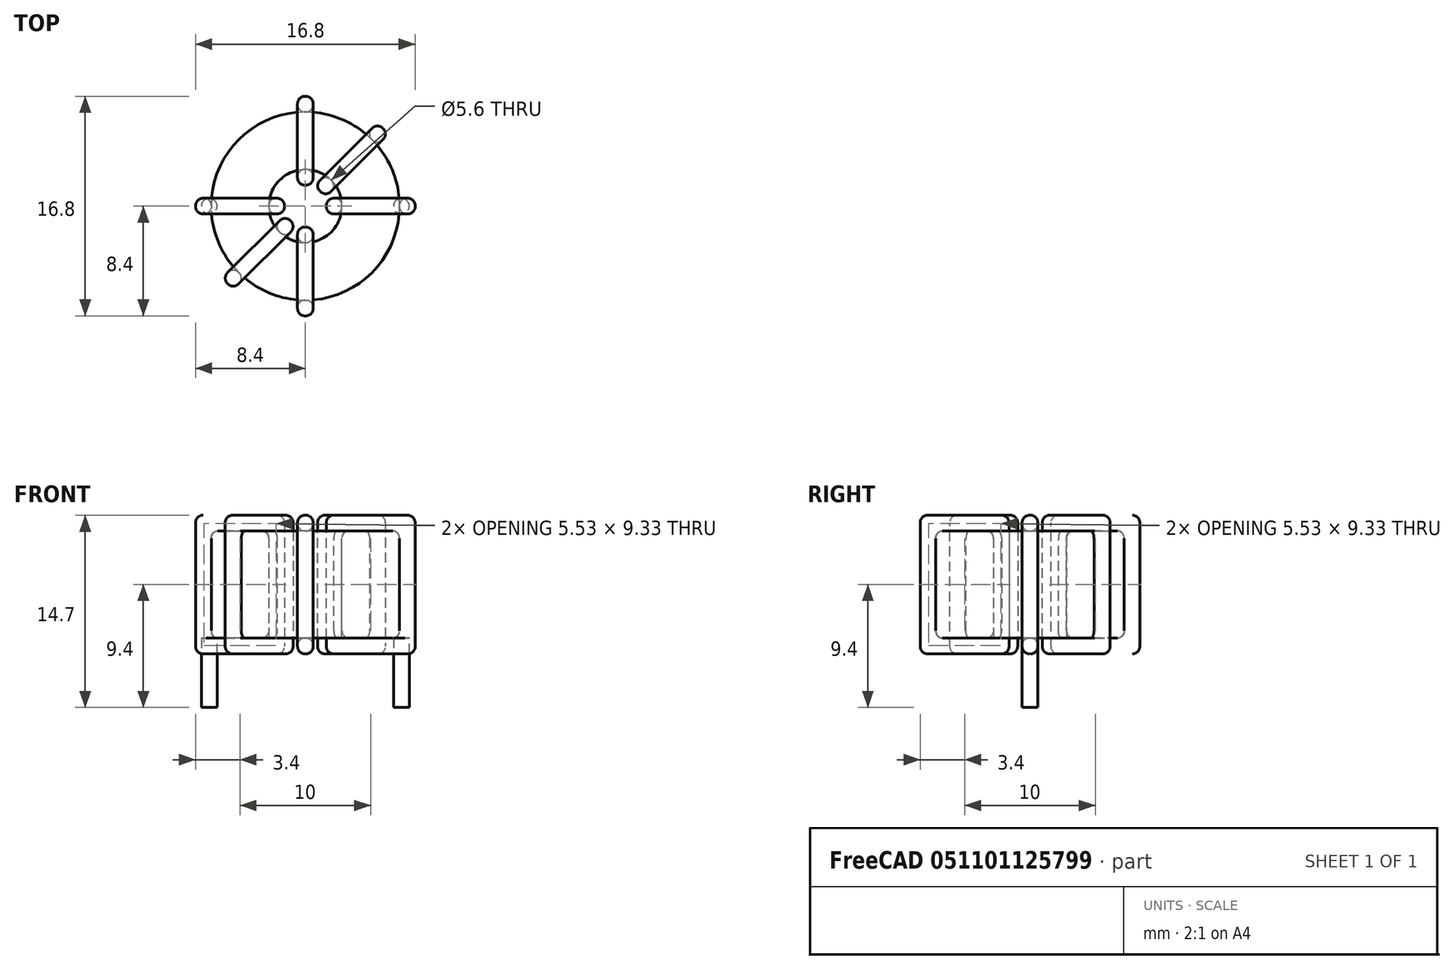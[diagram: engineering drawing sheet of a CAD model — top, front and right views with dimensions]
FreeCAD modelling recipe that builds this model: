
FCSTD DOCUMENT  (FreeCAD 0.16R6703 (Git))
Label: L_Toroid_Horizontal_D16.8mm_P14.70mm_Vishay_TJ3_BigPads
License: All rights reserved
LicenseURL: http://en.wikipedia.org/wiki/All_rights_reserved
objects: Sketcher::SketchObject×6, PartDesign::Pad×6, PartDesign::Fillet×5, Spreadsheet::Sheet×1
note: 23 computed .brp shape members not serialized (recipe doc carries the construction recipe); baked Part::Feature solids carry a one-line shape summary decoded from their .brp

FEATURE [Spreadsheet::Sheet] Spreadsheet  label="dimensions"
  cells = A1=Wx; B1(Wx)=16.8; C1(WW)=5.600000000000001; D1=16.8; A2=Wy; B2(Wy)=16.8; D2=16.8; A3=RM; B3(RMx)=14.7; C3(RMy)=0; A4=d_wire; B4(d_wire)=1.2; A5=H; B5(H)=8.199999999999999; A6=offsetx; B6(offsetx)=1.050000000000001
FEATURE [Sketcher::SketchObject] Sketch
  Placement = pos=(0,0,1.7) rot=(0,0,1;0rad)
  expr: Placement.Base.z = 0.5 + Spreadsheet.d_wire
  expr: Constraints[0] = Spreadsheet.Wx / 2 - Spreadsheet.d_wire
  expr: Constraints[4] = Spreadsheet.WW / 2
  expr: Constraints[2] = Spreadsheet.RMy / 2
  expr: Constraints[1] = Spreadsheet.RMx / 2
  sketch-geometry (2):
    g0: Circle CenterX=7.35 CenterY=0 CenterZ=0 NormalX=0 NormalY=0 NormalZ=1 Radius=7.2
    g1: Circle CenterX=7.35 CenterY=0 CenterZ=0 NormalX=0 NormalY=0 NormalZ=1 Radius=2.8
  constraints (5):
    c: Radius(g0) = 7.2
    c: DistanceX(g-1,g0) = 7.35
    c: DistanceY(g-1,g0) = 0
    c: Coincident(g1,g0)
    c: Radius(g1) = 2.8
FEATURE [PartDesign::Pad] Pad
  Length = 8.2
  Length2 = 100
  Placement = pos=(0,0,1.7) rot=(0,0,1;0rad)
  Sketch = -> Sketch
  Type = 0
  expr: Length = Spreadsheet.H
FEATURE [Sketcher::SketchObject] Sketch001
  Placement = pos=(0,0,1.1) rot=(0,0,1;0rad)
  expr: Placement.Base.z = 0.5 + Spreadsheet.d_wire * 0.5
  expr: Constraints[4] = Spreadsheet.RMx
  expr: Constraints[2] = Spreadsheet.RMy
  expr: Constraints[1] = Spreadsheet.d_wire / 2
  sketch-geometry (2):
    g0: Circle CenterX=0 CenterY=0 CenterZ=0 NormalX=0 NormalY=0 NormalZ=1 Radius=0.6
    g1: Circle CenterX=14.7 CenterY=0 CenterZ=0 NormalX=0 NormalY=0 NormalZ=1 Radius=0.6
  constraints (5):
    c: Equal(g0,g1)
    c: Radius(g0) = 0.6
    c: DistanceY(g-1,g1) = 0
    c: Coincident(g0,g-1)
    c: DistanceX(g-1,g1) = 14.7
FEATURE [PartDesign::Pad] Pad001
  Length = 0.6
  Length2 = 4.7
  Placement = pos=(0,0,1.1) rot=(0,0,1;0rad)
  Reversed = true
  Sketch = -> Sketch001
  Type = 4
  expr: Length2 = 3.5 + Spreadsheet.d_wire
  expr: Length = Spreadsheet.d_wire / 2
FEATURE [PartDesign::Fillet] Fillet
  Base = -> Pad [Edge6,Edge3,Edge2]
  Placement = pos=(0,0,1.7) rot=(0,0,1;0rad)
  Radius = 0.5
FEATURE [Sketcher::SketchObject] Sketch003
  Placement = pos=(7.35,0,0) rot=(1,0,0;1.5708rad)
  expr: Placement.Base.x = Spreadsheet.RMx / 2
  expr: Constraints[49] = Spreadsheet.Wx - Spreadsheet.d_wire * 2
  expr: Constraints[44] = Spreadsheet.d_wire
  expr: Constraints[23] = Spreadsheet.H
  expr: Constraints[22] = Spreadsheet.Wx / 2 - Spreadsheet.d_wire
  expr: Placement.Base.y = Spreadsheet.RMy / 2
  expr: Constraints[21] = (Spreadsheet.Wx - Spreadsheet.WW) / 2 - Spreadsheet.d_wire
  expr: Constraints[19] = Spreadsheet.d_wire
  expr: Constraints[17] = Spreadsheet.d_wire
  expr: Constraints[18] = Spreadsheet.d_wire
  expr: Constraints[16] = Spreadsheet.d_wire
  sketch-geometry (16):
    g0: LineSegment StartX=-1.6 StartY=0.5 StartZ=0 EndX=-8.4 EndY=0.5 EndZ=0
    g1: LineSegment StartX=-8.4 StartY=0.5 StartZ=0 EndX=-8.4 EndY=11.1 EndZ=0
    g2: LineSegment StartX=-8.4 StartY=11.1 StartZ=0 EndX=-1.6 EndY=11.1 EndZ=0
    g3: LineSegment StartX=-1.6 StartY=11.1 StartZ=0 EndX=-1.6 EndY=0.5 EndZ=0
    g4: LineSegment StartX=-7.2 StartY=9.9 StartZ=0 EndX=-2.8 EndY=9.9 EndZ=0
    g5: LineSegment StartX=-2.8 StartY=9.9 StartZ=0 EndX=-2.8 EndY=1.7 EndZ=0
    g6: LineSegment StartX=-2.8 StartY=1.7 StartZ=0 EndX=-7.2 EndY=1.7 EndZ=0
    g7: LineSegment StartX=-7.2 StartY=1.7 StartZ=0 EndX=-7.2 EndY=9.9 EndZ=0
    g8: LineSegment StartX=1.6 StartY=11.1 StartZ=0 EndX=8.4 EndY=11.1 EndZ=0
    g9: LineSegment StartX=8.4 StartY=11.1 StartZ=0 EndX=8.4 EndY=0.5 EndZ=0
    g10: LineSegment StartX=8.4 StartY=0.5 StartZ=0 EndX=1.6 EndY=0.5 EndZ=0
    g11: LineSegment StartX=1.6 StartY=0.5 StartZ=0 EndX=1.6 EndY=11.1 EndZ=0
    g12: LineSegment StartX=2.8 StartY=9.9 StartZ=0 EndX=7.2 EndY=9.9 EndZ=0
    g13: LineSegment StartX=7.2 StartY=9.9 StartZ=0 EndX=7.2 EndY=1.7 EndZ=0
    g14: LineSegment StartX=7.2 StartY=1.7 StartZ=0 EndX=2.8 EndY=1.7 EndZ=0
    g15: LineSegment StartX=2.8 StartY=1.7 StartZ=0 EndX=2.8 EndY=9.9 EndZ=0
  constraints (50):
    c: Horizontal(g0)
    c: Coincident(g1,g0)
    c: Vertical(g1)
    c: Coincident(g2,g1)
    c: Horizontal(g2)
    c: Coincident(g3,g2)
    c: Coincident(g3,g0)
    c: Vertical(g3)
    c: Coincident(g4,g5)
    c: Coincident(g5,g6)
    c: Coincident(g6,g7)
    c: Coincident(g7,g4)
    c: Horizontal(g4)
    c: Horizontal(g6)
    c: Vertical(g5)
    c: Vertical(g7)
    c: DistanceX(g1,g4) = 1.2
    c: DistanceY(g4,g1) = 1.2
    c: DistanceX(g5,g0) = 1.2
    c: DistanceY(g0,g5) = 1.2
    c: DistanceY(g-1,g0) = 0.5
    c: DistanceX(g6,g6) = 4.4
    c: DistanceX(g6,g-1) = 7.2
    c: DistanceY(g7,g7) = 8.2
    c: Coincident(g8,g9)
    c: Coincident(g9,g10)
    c: Coincident(g10,g11)
    c: Coincident(g11,g8)
    c: Horizontal(g8)
    c: Horizontal(g10)
    c: Vertical(g9)
    c: Vertical(g11)
    c: Coincident(g12,g13)
    c: Coincident(g13,g14)
    c: Coincident(g14,g15)
    c: Coincident(g15,g12)
    c: Horizontal(g12)
    c: Horizontal(g14)
    c: Vertical(g13)
    c: Vertical(g15)
    c: DistanceY(g8,g2) = 0
    c: DistanceY(g10,g0) = 0
    c: DistanceY(g14,g5) = 0
    c: DistanceY(g12,g4) = 0
    c: DistanceX(g8,g12) = 1.2
    c: Equal(g8,g2)
    c: Equal(g12,g4)
    c: Equal(g9,g1)
    c: Equal(g13,g7)
    c: DistanceX(g4,g12) = 14.4
FEATURE [PartDesign::Pad] Pad002
  Length = 1.2
  Length2 = 100
  Midplane = true
  Placement = pos=(7.35,0,0) rot=(1,0,0;1.5708rad)
  Sketch = -> Sketch003
  Type = 0
  expr: Length = Spreadsheet.d_wire
FEATURE [PartDesign::Fillet] Fillet001
  Base = -> Pad002 [Edge38,Edge41,Edge42,Edge43,Edge29,Edge32,Edge33,Edge34,Edge25,Edge35,Edge36,Edge13,Edge14,Edge15,Edge16,Edge17,Edge18,Edge19,Edge1,Edge2,Edge3,Edge4,Edge5,Edge6,Edge7,Edge37,Edge39,Edge40,Edge20,Edge23,Edge24,Edge21,Edge22,Edge8,Edge9,Edge10,Edge11,Edge12,Edge26,Edge27,+8 more]
  Placement = pos=(7.35,0,0) rot=(1,0,0;1.5708rad)
  Radius = 0.564
  expr: Radius = Spreadsheet.d_wire * 0.47
FEATURE [Sketcher::SketchObject] Sketch004
  Placement = pos=(7.35,0,0) rot=(0.862856,0.357407,0.357407;1.71777rad)
  expr: Placement.Base.x = Spreadsheet.RMx / 2
  expr: Constraints[49] = Spreadsheet.Wx - 2 * Spreadsheet.d_wire
  expr: Constraints[44] = Spreadsheet.d_wire
  expr: Constraints[23] = Spreadsheet.H
  expr: Constraints[22] = Spreadsheet.Wx / 2 - Spreadsheet.d_wire
  expr: Placement.Base.y = Spreadsheet.RMy / 2
  expr: Constraints[21] = (Spreadsheet.Wx - Spreadsheet.WW) / 2 - Spreadsheet.d_wire
  expr: Constraints[19] = Spreadsheet.d_wire
  expr: Constraints[17] = Spreadsheet.d_wire
  expr: Constraints[18] = Spreadsheet.d_wire
  expr: Constraints[16] = Spreadsheet.d_wire
  sketch-geometry (16):
    g0: LineSegment StartX=-1.6 StartY=0.5 StartZ=0 EndX=-8.4 EndY=0.5 EndZ=0
    g1: LineSegment StartX=-8.4 StartY=0.5 StartZ=0 EndX=-8.4 EndY=11.1 EndZ=0
    g2: LineSegment StartX=-8.4 StartY=11.1 StartZ=0 EndX=-1.6 EndY=11.1 EndZ=0
    g3: LineSegment StartX=-1.6 StartY=11.1 StartZ=0 EndX=-1.6 EndY=0.5 EndZ=0
    g4: LineSegment StartX=-7.2 StartY=9.9 StartZ=0 EndX=-2.8 EndY=9.9 EndZ=0
    g5: LineSegment StartX=-2.8 StartY=9.9 StartZ=0 EndX=-2.8 EndY=1.7 EndZ=0
    g6: LineSegment StartX=-2.8 StartY=1.7 StartZ=0 EndX=-7.2 EndY=1.7 EndZ=0
    g7: LineSegment StartX=-7.2 StartY=1.7 StartZ=0 EndX=-7.2 EndY=9.9 EndZ=0
    g8: LineSegment StartX=1.6 StartY=11.1 StartZ=0 EndX=8.4 EndY=11.1 EndZ=0
    g9: LineSegment StartX=8.4 StartY=11.1 StartZ=0 EndX=8.4 EndY=0.5 EndZ=0
    g10: LineSegment StartX=8.4 StartY=0.5 StartZ=0 EndX=1.6 EndY=0.5 EndZ=0
    g11: LineSegment StartX=1.6 StartY=0.5 StartZ=0 EndX=1.6 EndY=11.1 EndZ=0
    g12: LineSegment StartX=2.8 StartY=9.9 StartZ=0 EndX=7.2 EndY=9.9 EndZ=0
    g13: LineSegment StartX=7.2 StartY=9.9 StartZ=0 EndX=7.2 EndY=1.7 EndZ=0
    g14: LineSegment StartX=7.2 StartY=1.7 StartZ=0 EndX=2.8 EndY=1.7 EndZ=0
    g15: LineSegment StartX=2.8 StartY=1.7 StartZ=0 EndX=2.8 EndY=9.9 EndZ=0
  constraints (50):
    c: Horizontal(g0)
    c: Coincident(g1,g0)
    c: Vertical(g1)
    c: Coincident(g2,g1)
    c: Horizontal(g2)
    c: Coincident(g3,g2)
    c: Coincident(g3,g0)
    c: Vertical(g3)
    c: Coincident(g4,g5)
    c: Coincident(g5,g6)
    c: Coincident(g6,g7)
    c: Coincident(g7,g4)
    c: Horizontal(g4)
    c: Horizontal(g6)
    c: Vertical(g5)
    c: Vertical(g7)
    c: DistanceX(g1,g4) = 1.2
    c: DistanceY(g4,g1) = 1.2
    c: DistanceX(g5,g0) = 1.2
    c: DistanceY(g0,g5) = 1.2
    c: DistanceY(g-1,g0) = 0.5
    c: DistanceX(g6,g6) = 4.4
    c: DistanceX(g6,g-1) = 7.2
    c: DistanceY(g7,g7) = 8.2
    c: Coincident(g8,g9)
    c: Coincident(g9,g10)
    c: Coincident(g10,g11)
    c: Coincident(g11,g8)
    c: Horizontal(g8)
    c: Horizontal(g10)
    c: Vertical(g9)
    c: Vertical(g11)
    c: Coincident(g12,g13)
    c: Coincident(g13,g14)
    c: Coincident(g14,g15)
    c: Coincident(g15,g12)
    c: Horizontal(g12)
    c: Horizontal(g14)
    c: Vertical(g13)
    c: Vertical(g15)
    c: DistanceY(g8,g2) = 0
    c: DistanceY(g10,g0) = 0
    c: DistanceY(g14,g5) = 0
    c: DistanceY(g12,g4) = 0
    c: DistanceX(g8,g12) = 1.2
    c: Equal(g8,g2)
    c: Equal(g12,g4)
    c: Equal(g9,g1)
    c: Equal(g13,g7)
    c: DistanceX(g4,g12) = 14.4
FEATURE [PartDesign::Pad] Pad003
  Length = 1.2
  Length2 = 100
  Midplane = true
  Placement = pos=(7.35,0,0) rot=(0.862856,0.357407,0.357407;1.71777rad)
  Sketch = -> Sketch004
  Type = 0
  expr: Length = Spreadsheet.d_wire
FEATURE [PartDesign::Fillet] Fillet002
  Base = -> Pad003 [Edge38,Edge41,Edge42,Edge43,Edge29,Edge32,Edge33,Edge34,Edge25,Edge35,Edge36,Edge13,Edge14,Edge15,Edge16,Edge17,Edge18,Edge19,Edge1,Edge2,Edge3,Edge4,Edge5,Edge6,Edge7,Edge37,Edge39,Edge40,Edge20,Edge23,Edge24,Edge21,Edge22,Edge8,Edge9,Edge10,Edge11,Edge12,Edge26,Edge27,+8 more]
  Placement = pos=(7.35,0,0) rot=(0.862856,0.357407,0.357407;1.71777rad)
  Radius = 0.564
  expr: Radius = Spreadsheet.d_wire * 0.47
FEATURE [Sketcher::SketchObject] Sketch005
  Placement = pos=(7.35,0,0) rot=(0.862856,-0.357407,-0.357407;1.71777rad)
  expr: Placement.Base.x = Spreadsheet.RMx / 2
  expr: Constraints[49] = Spreadsheet.Wx - 2 * Spreadsheet.d_wire
  expr: Constraints[44] = Spreadsheet.d_wire
  expr: Constraints[23] = Spreadsheet.H
  expr: Constraints[22] = Spreadsheet.Wx / 2 - Spreadsheet.d_wire
  expr: Placement.Base.y = Spreadsheet.RMy / 2
  expr: Constraints[21] = (Spreadsheet.Wx - Spreadsheet.WW) / 2 - Spreadsheet.d_wire
  expr: Constraints[19] = Spreadsheet.d_wire
  expr: Constraints[17] = Spreadsheet.d_wire
  expr: Constraints[18] = Spreadsheet.d_wire
  expr: Constraints[16] = Spreadsheet.d_wire
  sketch-geometry (16):
    g0: LineSegment StartX=-1.6 StartY=0.5 StartZ=0 EndX=-8.4 EndY=0.5 EndZ=0
    g1: LineSegment StartX=-8.4 StartY=0.5 StartZ=0 EndX=-8.4 EndY=11.1 EndZ=0
    g2: LineSegment StartX=-8.4 StartY=11.1 StartZ=0 EndX=-1.6 EndY=11.1 EndZ=0
    g3: LineSegment StartX=-1.6 StartY=11.1 StartZ=0 EndX=-1.6 EndY=0.5 EndZ=0
    g4: LineSegment StartX=-7.2 StartY=9.9 StartZ=0 EndX=-2.8 EndY=9.9 EndZ=0
    g5: LineSegment StartX=-2.8 StartY=9.9 StartZ=0 EndX=-2.8 EndY=1.7 EndZ=0
    g6: LineSegment StartX=-2.8 StartY=1.7 StartZ=0 EndX=-7.2 EndY=1.7 EndZ=0
    g7: LineSegment StartX=-7.2 StartY=1.7 StartZ=0 EndX=-7.2 EndY=9.9 EndZ=0
    g8: LineSegment StartX=1.6 StartY=11.1 StartZ=0 EndX=8.4 EndY=11.1 EndZ=0
    g9: LineSegment StartX=8.4 StartY=11.1 StartZ=0 EndX=8.4 EndY=0.5 EndZ=0
    g10: LineSegment StartX=8.4 StartY=0.5 StartZ=0 EndX=1.6 EndY=0.5 EndZ=0
    g11: LineSegment StartX=1.6 StartY=0.5 StartZ=0 EndX=1.6 EndY=11.1 EndZ=0
    g12: LineSegment StartX=2.8 StartY=9.9 StartZ=0 EndX=7.2 EndY=9.9 EndZ=0
    g13: LineSegment StartX=7.2 StartY=9.9 StartZ=0 EndX=7.2 EndY=1.7 EndZ=0
    g14: LineSegment StartX=7.2 StartY=1.7 StartZ=0 EndX=2.8 EndY=1.7 EndZ=0
    g15: LineSegment StartX=2.8 StartY=1.7 StartZ=0 EndX=2.8 EndY=9.9 EndZ=0
  constraints (50):
    c: Horizontal(g0)
    c: Coincident(g1,g0)
    c: Vertical(g1)
    c: Coincident(g2,g1)
    c: Horizontal(g2)
    c: Coincident(g3,g2)
    c: Coincident(g3,g0)
    c: Vertical(g3)
    c: Coincident(g4,g5)
    c: Coincident(g5,g6)
    c: Coincident(g6,g7)
    c: Coincident(g7,g4)
    c: Horizontal(g4)
    c: Horizontal(g6)
    c: Vertical(g5)
    c: Vertical(g7)
    c: DistanceX(g1,g4) = 1.2
    c: DistanceY(g4,g1) = 1.2
    c: DistanceX(g5,g0) = 1.2
    c: DistanceY(g0,g5) = 1.2
    c: DistanceY(g-1,g0) = 0.5
    c: DistanceX(g6,g6) = 4.4
    c: DistanceX(g6,g-1) = 7.2
    c: DistanceY(g7,g7) = 8.2
    c: Coincident(g8,g9)
    c: Coincident(g9,g10)
    c: Coincident(g10,g11)
    c: Coincident(g11,g8)
    c: Horizontal(g8)
    c: Horizontal(g10)
    c: Vertical(g9)
    c: Vertical(g11)
    c: Coincident(g12,g13)
    c: Coincident(g13,g14)
    c: Coincident(g14,g15)
    c: Coincident(g15,g12)
    c: Horizontal(g12)
    c: Horizontal(g14)
    c: Vertical(g13)
    c: Vertical(g15)
    c: DistanceY(g8,g2) = 0
    c: DistanceY(g10,g0) = 0
    c: DistanceY(g14,g5) = 0
    c: DistanceY(g12,g4) = 0
    c: DistanceX(g8,g12) = 1.2
    c: Equal(g8,g2)
    c: Equal(g12,g4)
    c: Equal(g9,g1)
    c: Equal(g13,g7)
    c: DistanceX(g4,g12) = 14.4
FEATURE [PartDesign::Pad] Pad004
  Length = 1.2
  Length2 = 100
  Midplane = true
  Placement = pos=(7.35,0,0) rot=(0.862856,-0.357407,-0.357407;1.71777rad)
  Sketch = -> Sketch005
  Type = 0
  expr: Length = Spreadsheet.d_wire
FEATURE [PartDesign::Fillet] Fillet003
  Base = -> Pad004 [Edge38,Edge41,Edge42,Edge43,Edge29,Edge32,Edge33,Edge34,Edge25,Edge35,Edge36,Edge13,Edge14,Edge15,Edge16,Edge17,Edge18,Edge19,Edge1,Edge2,Edge3,Edge4,Edge5,Edge6,Edge7,Edge37,Edge39,Edge40,Edge20,Edge23,Edge24,Edge21,Edge22,Edge8,Edge9,Edge10,Edge11,Edge12,Edge26,Edge27,+8 more]
  Placement = pos=(7.35,0,0) rot=(0.862856,-0.357407,-0.357407;1.71777rad)
  Radius = 0.564
  expr: Radius = Spreadsheet.d_wire * 0.47
FEATURE [Sketcher::SketchObject] Sketch006
  Placement = pos=(7.35,0,0) rot=(0.57735,0.57735,0.57735;2.0944rad)
  expr: Placement.Base.x = Spreadsheet.RMx / 2
  expr: Constraints[49] = Spreadsheet.Wx - Spreadsheet.d_wire * 2
  expr: Constraints[44] = Spreadsheet.d_wire
  expr: Constraints[23] = Spreadsheet.H
  expr: Constraints[22] = Spreadsheet.Wx / 2 - Spreadsheet.d_wire
  expr: Placement.Base.y = Spreadsheet.RMy / 2
  expr: Constraints[21] = (Spreadsheet.Wx - Spreadsheet.WW) / 2 - Spreadsheet.d_wire
  expr: Constraints[19] = Spreadsheet.d_wire
  expr: Constraints[17] = Spreadsheet.d_wire
  expr: Constraints[18] = Spreadsheet.d_wire
  expr: Constraints[16] = Spreadsheet.d_wire
  sketch-geometry (16):
    g0: LineSegment StartX=-1.6 StartY=0.5 StartZ=0 EndX=-8.4 EndY=0.5 EndZ=0
    g1: LineSegment StartX=-8.4 StartY=0.5 StartZ=0 EndX=-8.4 EndY=11.1 EndZ=0
    g2: LineSegment StartX=-8.4 StartY=11.1 StartZ=0 EndX=-1.6 EndY=11.1 EndZ=0
    g3: LineSegment StartX=-1.6 StartY=11.1 StartZ=0 EndX=-1.6 EndY=0.5 EndZ=0
    g4: LineSegment StartX=-7.2 StartY=9.9 StartZ=0 EndX=-2.8 EndY=9.9 EndZ=0
    g5: LineSegment StartX=-2.8 StartY=9.9 StartZ=0 EndX=-2.8 EndY=1.7 EndZ=0
    g6: LineSegment StartX=-2.8 StartY=1.7 StartZ=0 EndX=-7.2 EndY=1.7 EndZ=0
    g7: LineSegment StartX=-7.2 StartY=1.7 StartZ=0 EndX=-7.2 EndY=9.9 EndZ=0
    g8: LineSegment StartX=1.6 StartY=11.1 StartZ=0 EndX=8.4 EndY=11.1 EndZ=0
    g9: LineSegment StartX=8.4 StartY=11.1 StartZ=0 EndX=8.4 EndY=0.5 EndZ=0
    g10: LineSegment StartX=8.4 StartY=0.5 StartZ=0 EndX=1.6 EndY=0.5 EndZ=0
    g11: LineSegment StartX=1.6 StartY=0.5 StartZ=0 EndX=1.6 EndY=11.1 EndZ=0
    g12: LineSegment StartX=2.8 StartY=9.9 StartZ=0 EndX=7.2 EndY=9.9 EndZ=0
    g13: LineSegment StartX=7.2 StartY=9.9 StartZ=0 EndX=7.2 EndY=1.7 EndZ=0
    g14: LineSegment StartX=7.2 StartY=1.7 StartZ=0 EndX=2.8 EndY=1.7 EndZ=0
    g15: LineSegment StartX=2.8 StartY=1.7 StartZ=0 EndX=2.8 EndY=9.9 EndZ=0
  constraints (50):
    c: Horizontal(g0)
    c: Coincident(g1,g0)
    c: Vertical(g1)
    c: Coincident(g2,g1)
    c: Horizontal(g2)
    c: Coincident(g3,g2)
    c: Coincident(g3,g0)
    c: Vertical(g3)
    c: Coincident(g4,g5)
    c: Coincident(g5,g6)
    c: Coincident(g6,g7)
    c: Coincident(g7,g4)
    c: Horizontal(g4)
    c: Horizontal(g6)
    c: Vertical(g5)
    c: Vertical(g7)
    c: DistanceX(g1,g4) = 1.2
    c: DistanceY(g4,g1) = 1.2
    c: DistanceX(g5,g0) = 1.2
    c: DistanceY(g0,g5) = 1.2
    c: DistanceY(g-1,g0) = 0.5
    c: DistanceX(g6,g6) = 4.4
    c: DistanceX(g6,g-1) = 7.2
    c: DistanceY(g7,g7) = 8.2
    c: Coincident(g8,g9)
    c: Coincident(g9,g10)
    c: Coincident(g10,g11)
    c: Coincident(g11,g8)
    c: Horizontal(g8)
    c: Horizontal(g10)
    c: Vertical(g9)
    c: Vertical(g11)
    c: Coincident(g12,g13)
    c: Coincident(g13,g14)
    c: Coincident(g14,g15)
    c: Coincident(g15,g12)
    c: Horizontal(g12)
    c: Horizontal(g14)
    c: Vertical(g13)
    c: Vertical(g15)
    c: DistanceY(g8,g2) = 0
    c: DistanceY(g10,g0) = 0
    c: DistanceY(g14,g5) = 0
    c: DistanceY(g12,g4) = 0
    c: DistanceX(g8,g12) = 1.2
    c: Equal(g8,g2)
    c: Equal(g12,g4)
    c: Equal(g9,g1)
    c: Equal(g13,g7)
    c: DistanceX(g4,g12) = 14.4
FEATURE [PartDesign::Pad] Pad005
  Length = 1.2
  Length2 = 100
  Midplane = true
  Placement = pos=(7.35,0,0) rot=(0.57735,0.57735,0.57735;2.0944rad)
  Sketch = -> Sketch006
  Type = 0
  expr: Length = Spreadsheet.d_wire
FEATURE [PartDesign::Fillet] Fillet004
  Base = -> Pad005 [Edge38,Edge41,Edge42,Edge43,Edge29,Edge32,Edge33,Edge34,Edge25,Edge35,Edge36,Edge13,Edge14,Edge15,Edge16,Edge17,Edge18,Edge19,Edge1,Edge2,Edge3,Edge4,Edge5,Edge6,Edge7,Edge37,Edge39,Edge40,Edge20,Edge23,Edge24,Edge21,Edge22,Edge8,Edge9,Edge10,Edge11,Edge12,Edge26,Edge27,+8 more]
  Placement = pos=(7.35,0,0) rot=(0.57735,0.57735,0.57735;2.0944rad)
  Radius = 0.564
  expr: Radius = Spreadsheet.d_wire * 0.47
